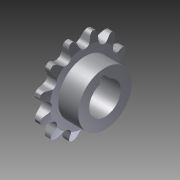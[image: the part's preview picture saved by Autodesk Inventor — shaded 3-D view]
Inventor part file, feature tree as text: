
AUTODESK INVENTOR PART (.ipt)
format: ipt  version: 2012 (Build 160160000, 160)  size: 369,664 bytes
history: native  units: in
note: dims shown in document units (in); Inventor stores cm internally (conversion verified against a paired STEP export)
features: sketch x2, extrude x2, revolve x1
ambient origin geometry x8: Origin, YZ Plane, XZ Plane, XY Plane, X Axis, Y Axis, Z Axis, Center Point
bodies: Solid1 (feature_tree)
feature tree (5):
  revolve  "Revolution1"  [1 undecoded]
  sketch  "Sketch3"  dims[d3=0.55in d4=0.3346in d5=90.0deg d12=0.25in d26=30.0deg d27=0.0649in d29=4.7244in d30=0.0684in d31=0.483in d32=0.0469in d33=0.0684in d34=0.125in d35=360.0deg d36=0.25in d37=0.55in d38=1.1in d39=1.0in d40=0.0in d41=0.125in d42=0.125in d43=0.0625in d44=0.3937in d45=0.2594in d46=1.0in d47=0.0in]
  extrude  "Extrusion2"  Depth=0.3346in
  extrude  "Extrusion3"  TaperAngle=90.0deg  [1 undecoded]
  sketch  "Sketch1"  dims[d0=0.125in d1=0.1969in]
note: 2 required parameter values undecoded (feature->parameter linkage not recoverable at this tier; creation-order binding heuristic only, values carry confidence <= 0.55)